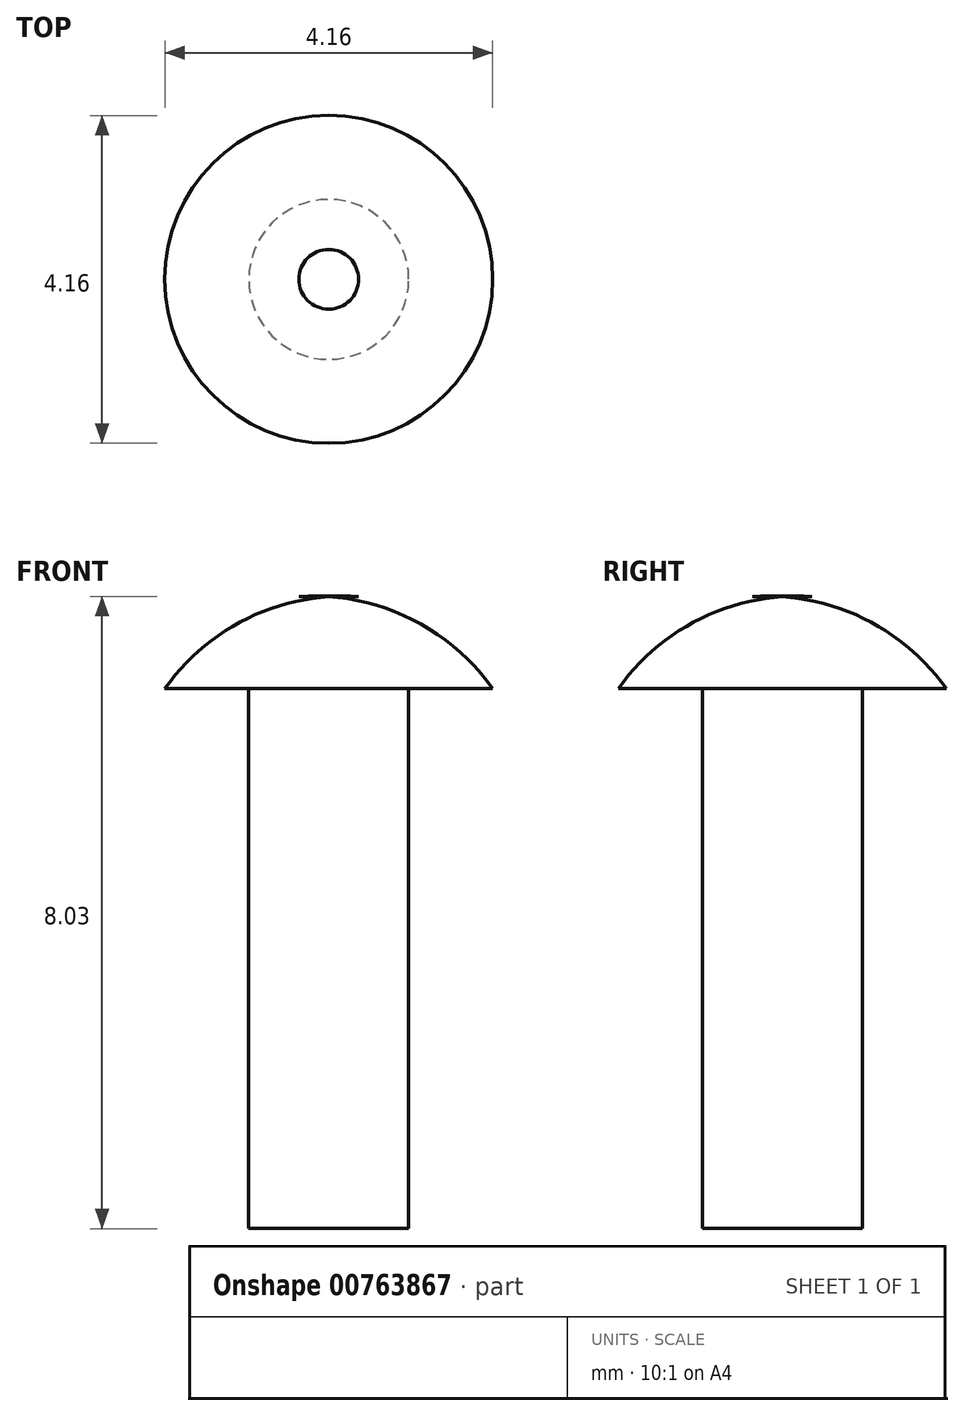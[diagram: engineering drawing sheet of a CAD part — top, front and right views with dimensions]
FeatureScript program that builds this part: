
annotation { "Feature Type Name" : "Feature", "Feature Type Description" : "" }
export const myFeature = defineFeature(function(context is Context, id is Id, definition is map)
    precondition{}
    {
        {
            var Q0;
            Q0=qCreatedBy(makeId("Top.planeOp"),FACE);
            var sketch = newSketch(context, id + "F0", { "sketchPlane" : qUnion([Q0])});
            skCircle(sketch, "E0", {"center": v(0, 0) * mm, "radius": 1.02 * mm});
            skSolve(sketch);
        }
        {
            var Q0;
            Q0=qSketchRegion(id+"F0",true);
            extrude(context, id + "F1", {"entities" : qUnion([Q0]), "oppositeDirection" : true, "depth" : 6.86 * mm, "offsetDistance" : 25.4 * mm});
        }
        {
            var Q0;
            Q0=qCreatedBy(makeId("Front.planeOp"),FACE);
            var sketch = newSketch(context, id + "F2", { "sketchPlane" : qUnion([Q0])});
            skLineSegment(sketch, "E1", {"start": v(0, 0) * mm, "end": v(-2.08, 0) * mm});
            skLineSegment(sketch, "E2", {"start": v(0, 0) * mm, "end": v(0, 1.17) * mm});
            skArc(sketch, "E3", {"start": v(0, 1.17) * mm, "mid": v(-1.17, 0.82) * mm, "end": v(-2.08, 0) * mm});
            skSolve(sketch);
        }
        {
            var Q0;
            Q0=makeQuery(id+"F2.imprint","IMPRINT",FACE,{"disambiguationData":[TD([[makeQuery(id+"F2.imprint","IMPRINT",EDGE,{"derivedFrom":sQuery(id+"F2.wireOp",EDGE,"E1")}),-1.0]])]});
            var Q1;
            Q1=sQuery(id+"F2.wireOp",EDGE,"E2");
            revolve(context, id + "F3", {"operationType" : NewBodyOperationType.ADD, "surfaceOperationType" : NewSurfaceOperationType.NEW, "entities" : qUnion([Q0]), "axis" : qUnion([Q1]), "revolveType" : RevolveType.FULL});
        }
    });
